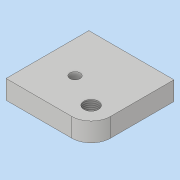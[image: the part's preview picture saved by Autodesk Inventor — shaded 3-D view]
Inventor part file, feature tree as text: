
AUTODESK INVENTOR PART (.ipt)
format: ipt  version: 2022 (Build 260153000, 153)  size: 119,296 bytes
history: native  units: mm
features: sketch x5, hole x2, extrude x1, fillet x1
ambient origin geometry x8: Origin, YZ Plane, XZ Plane, XY Plane, X Axis, Y Axis, Z Axis, Center Point
bodies: Body1 (feature_tree)
feature tree (9):
  extrude  "Выдавливание2"  TaperAngle=0.0deg  [1 undecoded]
  fillet  "Сопряжение1"  Radius=42.0mm
  hole  "Отверстие5"  [1 undecoded]
  hole  "Отверстие7"  [1 undecoded]
  sketch  "Эскиз1"
  sketch  "Эскиз2"
  sketch  "Эскиз3"
  sketch  "Эскиз5"
  sketch  "Эскиз7"
note: 3 required parameter values undecoded (feature->parameter linkage not recoverable at this tier; creation-order binding heuristic only, values carry confidence <= 0.55)
